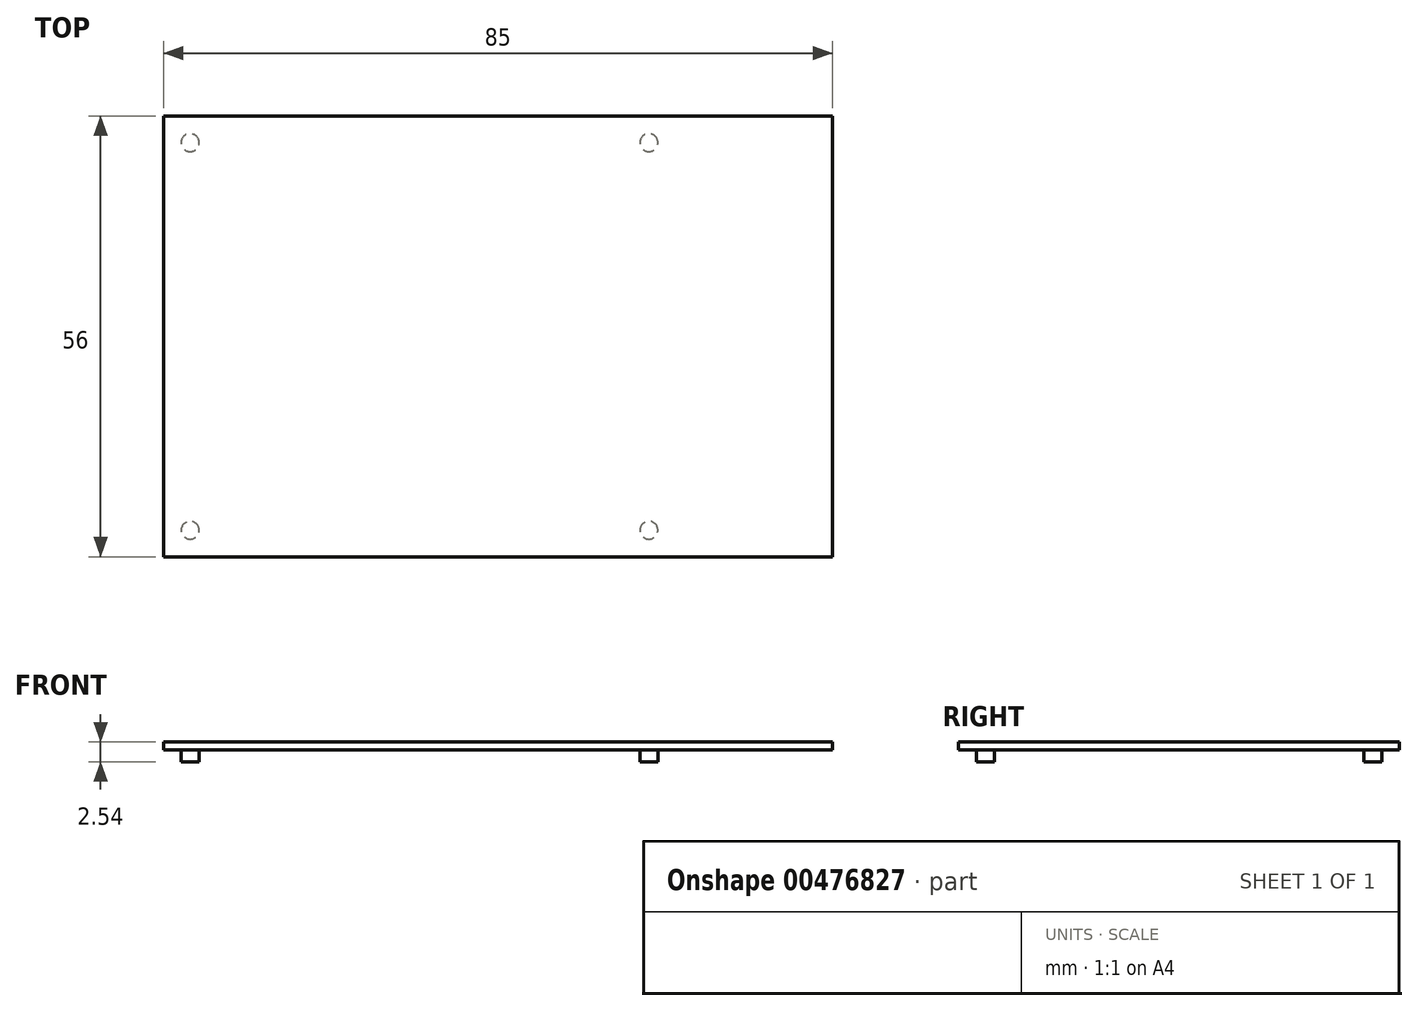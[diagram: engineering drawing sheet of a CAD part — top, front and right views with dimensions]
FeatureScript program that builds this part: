
annotation { "Feature Type Name" : "Feature", "Feature Type Description" : "" }
export const myFeature = defineFeature(function(context is Context, id is Id, definition is map)
    precondition{}
    {
        {
            var Q0;
            Q0=qCreatedBy(makeId("Top.planeOp"),FACE);
            var sketch = newSketch(context, id + "F0", { "sketchPlane" : qUnion([Q0])});
            skLineSegment(sketch, "E0.bottom", {"start": v(42.5, 28) * mm, "end": v(-42.5, 28) * mm});
            skLineSegment(sketch, "E0.top", {"start": v(42.5, -28) * mm, "end": v(-42.5, -28) * mm});
            skLineSegment(sketch, "E0.left", {"start": v(42.5, 28) * mm, "end": v(42.5, -28) * mm});
            skLineSegment(sketch, "E0.right", {"start": v(-42.5, 28) * mm, "end": v(-42.5, -28) * mm});
            skPoint(sketch, "E0.middle", {"position": v(0, 0) * mm});
            skCircle(sketch, "E1", {"center": v(-39.11, -24.62) * mm, "radius": 1.14 * mm});
            skCircle(sketch, "E2", {"center": v(-39.12, 24.62) * mm, "radius": 1.14 * mm});
            skCircle(sketch, "E3", {"center": v(19.16, -24.62) * mm, "radius": 1.14 * mm});
            skCircle(sketch, "E4", {"center": v(0, 0) * mm, "radius": 1.14 * mm});
            skCircle(sketch, "E5", {"center": v(19.16, 24.62) * mm, "radius": 1.14 * mm});
            skLineSegment(sketch, "E6", {"start": v(-42.5, -28) * mm, "end": v(42.5, -28) * mm});
            skLineSegment(sketch, "E7", {"start": v(42.5, -28) * mm, "end": v(223.86, -28) * mm});
            skLineSegment(sketch, "E8", {"start": v(223.86, -28) * mm, "end": v(223.86, 149.84) * mm});
            skLineSegment(sketch, "E9", {"start": v(223.86, 149.84) * mm, "end": v(42.5, 149.84) * mm});
            skLineSegment(sketch, "E10", {"start": v(42.5, 149.84) * mm, "end": v(-104.7, 149.84) * mm});
            skLineSegment(sketch, "E11", {"start": v(-104.7, 149.84) * mm, "end": v(-104.7, -28) * mm});
            skLineSegment(sketch, "E12", {"start": v(-104.7, -28) * mm, "end": v(-42.5, -28) * mm});
            skSolve(sketch);
        }
        {
            var Q0;
            Q0=makeQuery(id+"F0.imprint","IMPRINT",FACE,{"disambiguationData":[TD([[makeQuery(id+"F0.imprint","IMPRINT",EDGE,{"derivedFrom":sQuery(id+"F0.wireOp",EDGE,"E4")}),1.0]])]});
            var Q1;
            Q1=makeQuery(id+"F0.imprint","IMPRINT",FACE,{"disambiguationData":[TD([[makeQuery(id+"F0.imprint","IMPRINT",EDGE,{"derivedFrom":sQuery(id+"F0.wireOp",EDGE,"E0.bottom")}),1.0]])]});
            extrude(context, id + "F1", {"entities" : qUnion([Q0, Q1]), "depth" : 1.02 * mm});
        }
        {
            var Q0;
            Q0=makeQuery(id+"F1.opExtrude","CAP_FACE",FACE,{"disambiguationData":[OSD([sQuery(id+"F0.wireOp",EDGE,"E0.bottom"),sQuery(id+"F0.wireOp",EDGE,"E0.left"),sQuery(id+"F0.wireOp",EDGE,"E0.right"),sQuery(id+"F0.wireOp",EDGE,"E1"),sQuery(id+"F0.wireOp",EDGE,"E2"),sQuery(id+"F0.wireOp",EDGE,"E3"),sQuery(id+"F0.wireOp",EDGE,"E5"),sQuery(id+"F0.wireOp",EDGE,"E6")])],"isStart":false});
            var sketch = newSketch(context, id + "F2", { "sketchPlane" : qUnion([Q0])});
            skCircle(sketch, "E13.0", {"center": v(19.16, 24.62) * mm, "radius": 1.14 * mm});
            skCircle(sketch, "E14.0", {"center": v(-39.12, 24.62) * mm, "radius": 1.14 * mm});
            skCircle(sketch, "E15.0", {"center": v(19.16, -24.62) * mm, "radius": 1.14 * mm});
            skCircle(sketch, "E16.0", {"center": v(-39.11, -24.62) * mm, "radius": 1.14 * mm});
            skSolve(sketch);
        }
        {
            var Q0;
            Q0 = qSketchRegion(id + "F2", true);
            extrude(context, id + "F3", {"entities" : qUnion([Q0]), "operationType" : NewBodyOperationType.ADD, "oppositeDirection" : true, "depth" : 2.54 * mm});
        }
    });
